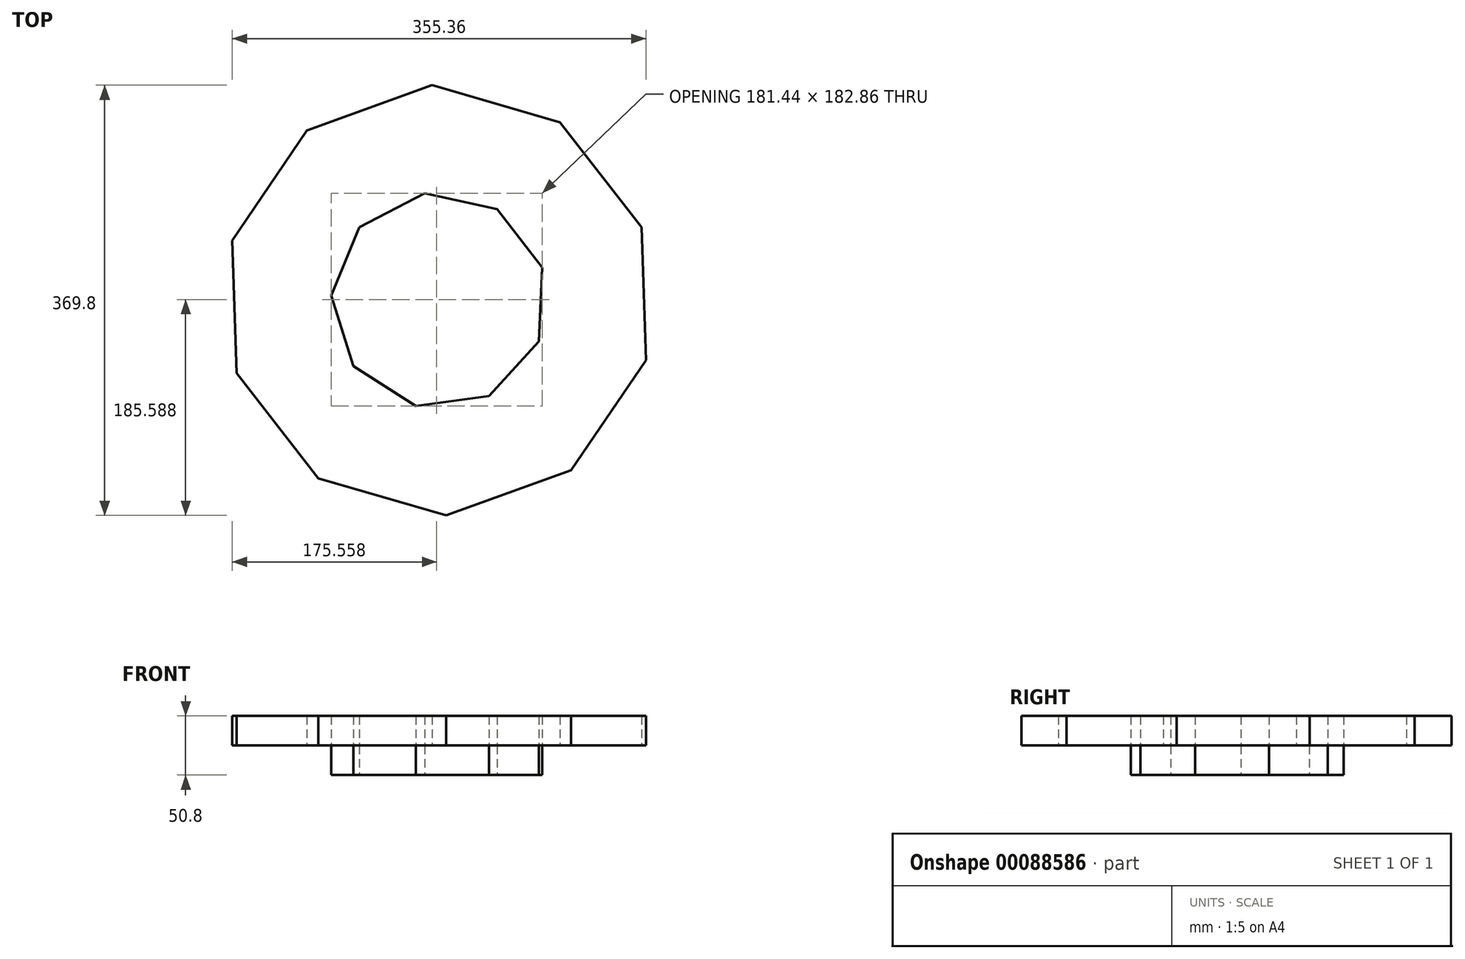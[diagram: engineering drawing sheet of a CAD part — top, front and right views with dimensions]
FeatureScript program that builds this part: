
annotation { "Feature Type Name" : "Feature", "Feature Type Description" : "" }
export const myFeature = defineFeature(function(context is Context, id is Id, definition is map)
    precondition{}
    {
        {
            var Q0;
            Q0=qCreatedBy(makeId("Top.planeOp"),FACE);
            var sketch = newSketch(context, id + "F0", { "sketchPlane" : qUnion([Q0])});
            skCircle(sketch, "E0.cCircle", {"center": v(0, 0) * mm, "radius": 87.32 * mm, "construction": true});
            skLineSegment(sketch, "E0.0", {"start": v(85.89, -35.48) * mm, "end": v(42.99, -82.38) * mm});
            skLineSegment(sketch, "E0.1", {"start": v(42.99, -82.38) * mm, "end": v(-20.02, -90.74) * mm});
            skLineSegment(sketch, "E0.2", {"start": v(-20.02, -90.74) * mm, "end": v(-73.67, -56.64) * mm});
            skLineSegment(sketch, "E0.3", {"start": v(-73.67, -56.64) * mm, "end": v(-92.84, 3.96) * mm});
            skLineSegment(sketch, "E0.4", {"start": v(-92.84, 3.96) * mm, "end": v(-68.57, 62.71) * mm});
            skLineSegment(sketch, "E0.5", {"start": v(-68.57, 62.71) * mm, "end": v(-12.22, 92.12) * mm});
            skLineSegment(sketch, "E0.6", {"start": v(-12.22, 92.12) * mm, "end": v(49.85, 78.42) * mm});
            skLineSegment(sketch, "E0.7", {"start": v(49.85, 78.42) * mm, "end": v(88.6, 28.03) * mm});
            skLineSegment(sketch, "E0.8", {"start": v(88.6, 28.03) * mm, "end": v(85.89, -35.48) * mm});
            skPoint(sketch, "E0.0.midPoint", {"position": v(64.44, -58.93) * mm});
            skSolve(sketch);
        }
        {
            var Q0;
            Q0 = qSketchRegion(id + "F0", true);
            extrude(context, id + "F1", {"entities" : qUnion([Q0]), "depth" : 25.4 * mm});
        }
        {
            var Q0;
            Q0=makeQuery(id+"F1.opExtrude","CAP_FACE",FACE,{"disambiguationData":[OSD([sQuery(id+"F0.wireOp",EDGE,"E0.0"),sQuery(id+"F0.wireOp",EDGE,"E0.1"),sQuery(id+"F0.wireOp",EDGE,"E0.2"),sQuery(id+"F0.wireOp",EDGE,"E0.3"),sQuery(id+"F0.wireOp",EDGE,"E0.4"),sQuery(id+"F0.wireOp",EDGE,"E0.5"),sQuery(id+"F0.wireOp",EDGE,"E0.6"),sQuery(id+"F0.wireOp",EDGE,"E0.7"),sQuery(id+"F0.wireOp",EDGE,"E0.8")])],"isStart":false});
            var sketch = newSketch(context, id + "F2", { "sketchPlane" : qUnion([Q0])});
            skCircle(sketch, "E1.cCircle", {"center": v(0, 0) * mm, "radius": 175.94 * mm, "construction": true});
            skLineSegment(sketch, "E1.0", {"start": v(177.68, -51.5) * mm, "end": v(113.48, -146.1) * mm});
            skLineSegment(sketch, "E1.1", {"start": v(113.48, -146.1) * mm, "end": v(5.93, -184.9) * mm});
            skLineSegment(sketch, "E1.2", {"start": v(5.93, -184.9) * mm, "end": v(-103.88, -153.07) * mm});
            skLineSegment(sketch, "E1.3", {"start": v(-103.88, -153.07) * mm, "end": v(-174.01, -62.78) * mm});
            skLineSegment(sketch, "E1.4", {"start": v(-174.01, -62.78) * mm, "end": v(-177.68, 51.5) * mm});
            skLineSegment(sketch, "E1.5", {"start": v(-177.68, 51.5) * mm, "end": v(-113.48, 146.1) * mm});
            skLineSegment(sketch, "E1.6", {"start": v(-113.48, 146.1) * mm, "end": v(-5.93, 184.9) * mm});
            skLineSegment(sketch, "E1.7", {"start": v(-5.93, 184.9) * mm, "end": v(103.88, 153.07) * mm});
            skLineSegment(sketch, "E1.8", {"start": v(103.88, 153.07) * mm, "end": v(174.01, 62.78) * mm});
            skLineSegment(sketch, "E1.9", {"start": v(174.01, 62.78) * mm, "end": v(177.68, -51.5) * mm});
            skPoint(sketch, "E1.0.midPoint", {"position": v(145.58, -98.8) * mm});
            skSolve(sketch);
        }
        {
            var Q0;
            Q0=makeQuery(id+"F2.imprint","IMPRINT",FACE,{"disambiguationData":[TD([[makeQuery(id+"F2.imprint","IMPRINT",EDGE,{"derivedFrom":sQuery(id+"F2.wireOp",EDGE,"E1.0")}),-1.0]])]});
            extrude(context, id + "F3", {"entities" : qUnion([Q0]), "depth" : 25.4 * mm});
        }
        {
            var Q0;
            Q0=makeQuery(id+"F1.opExtrude","CAP_FACE",FACE,{"disambiguationData":[OSD([sQuery(id+"F0.wireOp",EDGE,"E0.0"),sQuery(id+"F0.wireOp",EDGE,"E0.1"),sQuery(id+"F0.wireOp",EDGE,"E0.2"),sQuery(id+"F0.wireOp",EDGE,"E0.3"),sQuery(id+"F0.wireOp",EDGE,"E0.4"),sQuery(id+"F0.wireOp",EDGE,"E0.5"),sQuery(id+"F0.wireOp",EDGE,"E0.6"),sQuery(id+"F0.wireOp",EDGE,"E0.7"),sQuery(id+"F0.wireOp",EDGE,"E0.8")])],"isStart":false});
            extrude(context, id + "F4", {"entities" : qUnion([Q0]), "depth" : 25.4 * mm});
        }
    });
